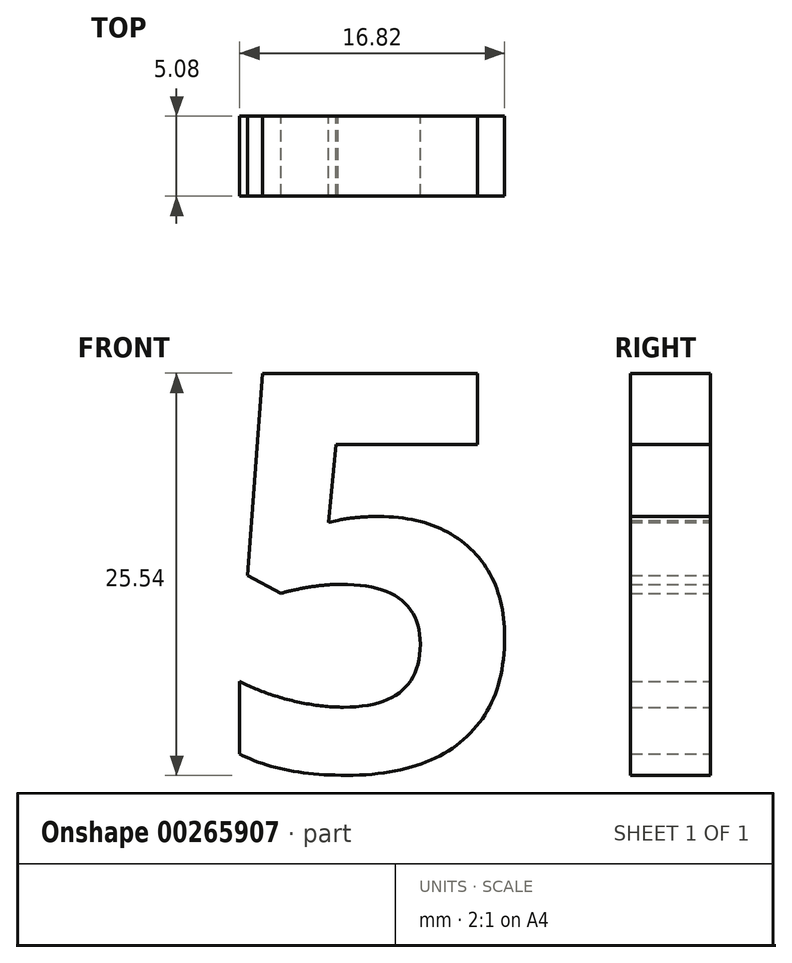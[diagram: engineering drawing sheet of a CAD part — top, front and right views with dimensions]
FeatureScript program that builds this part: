
annotation { "Feature Type Name" : "Feature", "Feature Type Description" : "" }
export const myFeature = defineFeature(function(context is Context, id is Id, definition is map)
    precondition{}
    {
        {
            var Q0;
            Q0=qCreatedBy(makeId("Front.planeOp"),FACE);
            var sketch = newSketch(context, id + "F0", { "sketchPlane" : qUnion([Q0])});
            skText(sketch, "E0", { "text": "5", "fontName": "OpenSans-Bold.ttf"});
            const initialGuessF0  = {"E0": [-0.0915, -0.01438, 1, 0, 0.0254]};
            skSetInitialGuess(sketch, initialGuessF0);
            skSolve(sketch);
        }
        {
            var Q0;
            Q0 = qSketchRegion(id + "F0", true);
            extrude(context, id + "F1", {"entities" : qUnion([Q0]), "depth" : 5.08 * mm});
        }
    });
